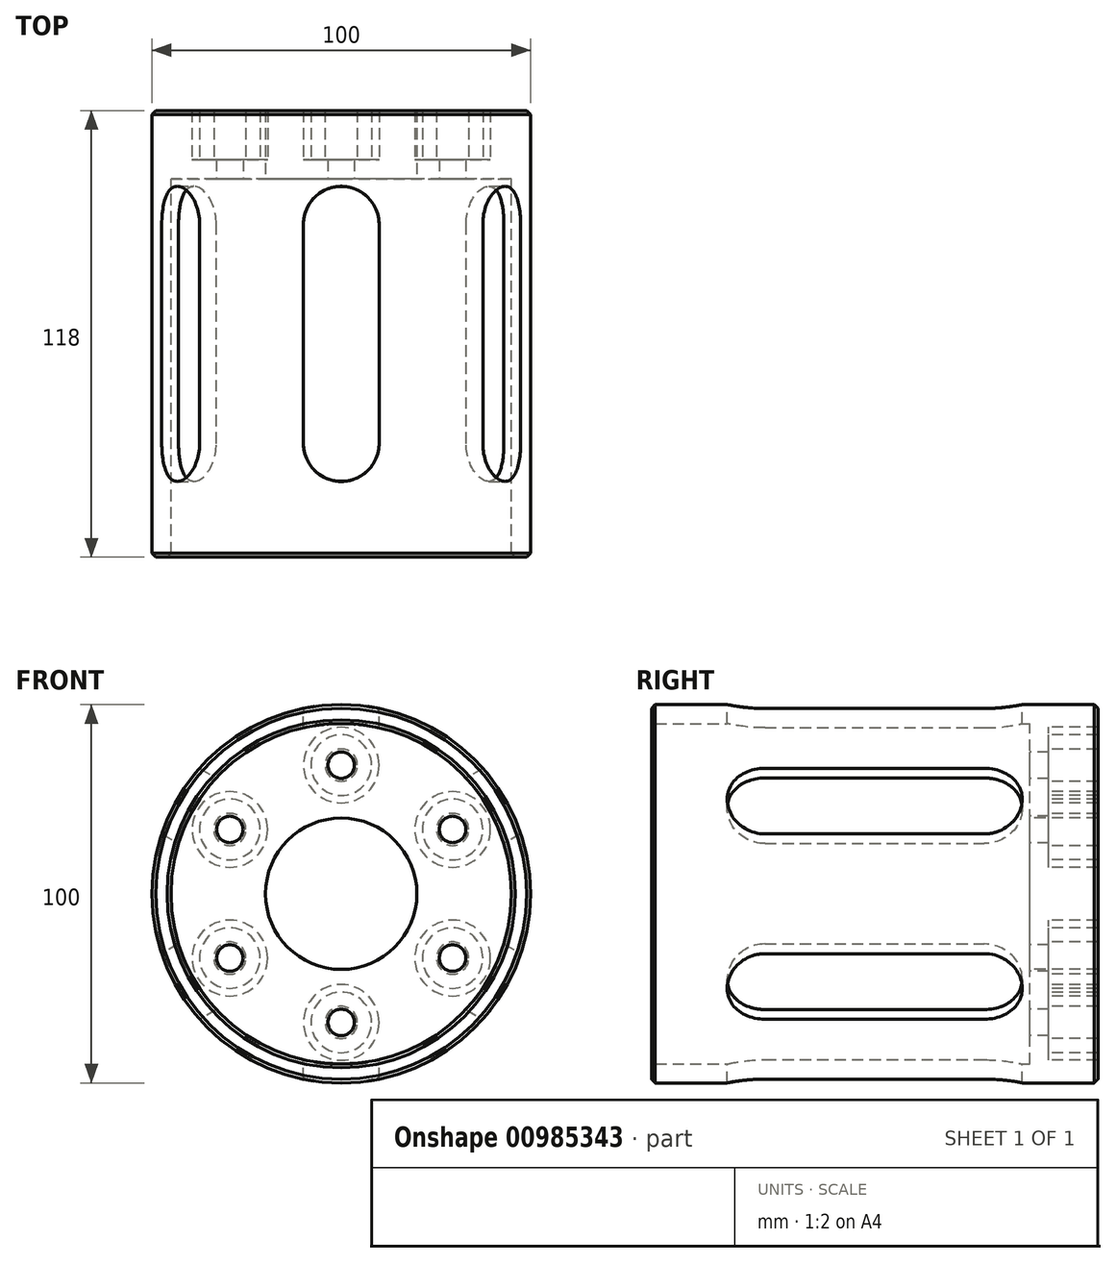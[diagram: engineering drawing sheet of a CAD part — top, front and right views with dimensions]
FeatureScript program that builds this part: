
annotation { "Feature Type Name" : "Feature", "Feature Type Description" : "" }
export const myFeature = defineFeature(function(context is Context, id is Id, definition is map)
    precondition{}
    {
        {
            var Q0;
            Q0=qCreatedBy(makeId("Top.planeOp"),FACE);
            var sketch = newSketch(context, id + "F0", { "sketchPlane" : qUnion([Q0])});
            skLineSegment(sketch, "E0", {"start": v(0, 60.4) * mm, "end": v(0, -60.4) * mm, "construction": true});
            skSolve(sketch);
        }
        {
            var Q0;
            Q0=qCreatedBy(makeId("Front.planeOp"),FACE);
            var sketch = newSketch(context, id + "F1", { "sketchPlane" : qUnion([Q0])});
            skCircle(sketch, "E1", {"center": v(0, 0) * mm, "radius": 50 * mm});
            skCircle(sketch, "E2", {"center": v(0, 34) * mm, "radius": 10 * mm});
            skCircle(sketch, "E3", {"center": v(0, 34) * mm, "radius": 4.25 * mm});
            skCircle(sketch, "E4", {"center": v(0, 34) * mm, "radius": 8 * mm});
            skCircle(sketch, "E5", {"center": v(0, 0) * mm, "radius": 20 * mm});
            skCircle(sketch, "E6", {"center": v(0, 0) * mm, "radius": 45 * mm});
            skCircle(sketch, "E7", {"center": v(0, 34) * mm, "radius": 3.5 * mm});
            skCircle(sketch, "E8.1.0", {"center": v(-29.44, 17) * mm, "radius": 3.5 * mm});
            skCircle(sketch, "E8.1.1", {"center": v(-29.44, 17) * mm, "radius": 4.25 * mm});
            skCircle(sketch, "E8.1.2", {"center": v(-29.44, 17) * mm, "radius": 10 * mm});
            skCircle(sketch, "E8.1.3", {"center": v(-29.44, 17) * mm, "radius": 8 * mm});
            skCircle(sketch, "E8.2.0", {"center": v(-29.44, -17) * mm, "radius": 3.5 * mm});
            skCircle(sketch, "E8.2.1", {"center": v(-29.44, -17) * mm, "radius": 4.25 * mm});
            skCircle(sketch, "E8.2.2", {"center": v(-29.44, -17) * mm, "radius": 10 * mm});
            skCircle(sketch, "E8.2.3", {"center": v(-29.44, -17) * mm, "radius": 8 * mm});
            skCircle(sketch, "E8.3.0", {"center": v(0, -34) * mm, "radius": 3.5 * mm});
            skCircle(sketch, "E8.3.1", {"center": v(0, -34) * mm, "radius": 4.25 * mm});
            skCircle(sketch, "E8.3.2", {"center": v(0, -34) * mm, "radius": 10 * mm});
            skCircle(sketch, "E8.3.3", {"center": v(0, -34) * mm, "radius": 8 * mm});
            skCircle(sketch, "E8.4.0", {"center": v(29.44, -17) * mm, "radius": 3.5 * mm});
            skCircle(sketch, "E8.4.1", {"center": v(29.44, -17) * mm, "radius": 4.25 * mm});
            skCircle(sketch, "E8.4.2", {"center": v(29.44, -17) * mm, "radius": 10 * mm});
            skCircle(sketch, "E8.4.3", {"center": v(29.44, -17) * mm, "radius": 8 * mm});
            skCircle(sketch, "E8.5.0", {"center": v(29.44, 17) * mm, "radius": 3.5 * mm});
            skCircle(sketch, "E8.5.1", {"center": v(29.44, 17) * mm, "radius": 4.25 * mm});
            skCircle(sketch, "E8.5.2", {"center": v(29.44, 17) * mm, "radius": 10 * mm});
            skCircle(sketch, "E8.5.3", {"center": v(29.44, 17) * mm, "radius": 8 * mm});
            skSolve(sketch);
        }
        {
            var Q0;
            Q0=makeQuery(id+"F1.imprint","IMPRINT",FACE,{"disambiguationData":[TD([[makeQuery(id+"F1.imprint","IMPRINT",EDGE,{"derivedFrom":sQuery(id+"F1.wireOp",EDGE,"E2")}),-1.0]])]});
            var Q1;
            Q1=makeQuery(id+"F1.imprint","IMPRINT",FACE,{"disambiguationData":[TD([[makeQuery(id+"F1.imprint","IMPRINT",EDGE,{"derivedFrom":sQuery(id+"F1.wireOp",EDGE,"E8.1.1")}),-1.0]])]});
            var Q2;
            Q2=makeQuery(id+"F1.imprint","IMPRINT",FACE,{"disambiguationData":[TD([[makeQuery(id+"F1.imprint","IMPRINT",EDGE,{"derivedFrom":sQuery(id+"F1.wireOp",EDGE,"E3")}),-1.0]])]});
            var Q3;
            Q3=makeQuery(id+"F1.imprint","IMPRINT",FACE,{"disambiguationData":[TD([[makeQuery(id+"F1.imprint","IMPRINT",EDGE,{"derivedFrom":sQuery(id+"F1.wireOp",EDGE,"E8.5.1")}),-1.0]])]});
            var Q4;
            Q4=makeQuery(id+"F1.imprint","IMPRINT",FACE,{"disambiguationData":[TD([[makeQuery(id+"F1.imprint","IMPRINT",EDGE,{"derivedFrom":sQuery(id+"F1.wireOp",EDGE,"E8.2.1")}),-1.0]])]});
            var Q5;
            Q5=makeQuery(id+"F1.imprint","IMPRINT",FACE,{"disambiguationData":[TD([[makeQuery(id+"F1.imprint","IMPRINT",EDGE,{"derivedFrom":sQuery(id+"F1.wireOp",EDGE,"E8.3.1")}),-1.0]])]});
            var Q6;
            Q6=makeQuery(id+"F1.imprint","IMPRINT",FACE,{"disambiguationData":[TD([[makeQuery(id+"F1.imprint","IMPRINT",EDGE,{"derivedFrom":sQuery(id+"F1.wireOp",EDGE,"E8.4.1")}),-1.0]])]});
            var Q7;
            Q7=makeQuery(id+"F1.imprint","IMPRINT",FACE,{"disambiguationData":[TD([[makeQuery(id+"F1.imprint","IMPRINT",EDGE,{"derivedFrom":sQuery(id+"F1.wireOp",EDGE,"E1")}),1.0]])]});
            extrude(context, id + "F2", {"entities" : qUnion([Q0, Q1, Q2, Q3, Q4, Q5, Q6, Q7]), "oppositeDirection" : true, "depth" : 18 * mm});
        }
        {
            var Q0;
            Q0=makeQuery(id+"F1.imprint","IMPRINT",FACE,{"disambiguationData":[TD([[makeQuery(id+"F1.imprint","IMPRINT",EDGE,{"derivedFrom":sQuery(id+"F1.wireOp",EDGE,"E2")}),1.0]])]});
            var Q1;
            Q1=makeQuery(id+"F1.imprint","IMPRINT",FACE,{"disambiguationData":[TD([[makeQuery(id+"F1.imprint","IMPRINT",EDGE,{"derivedFrom":sQuery(id+"F1.wireOp",EDGE,"E8.1.2")}),1.0]])]});
            var Q2;
            Q2=makeQuery(id+"F1.imprint","IMPRINT",FACE,{"disambiguationData":[TD([[makeQuery(id+"F1.imprint","IMPRINT",EDGE,{"derivedFrom":sQuery(id+"F1.wireOp",EDGE,"E8.2.2")}),1.0]])]});
            var Q3;
            Q3=makeQuery(id+"F1.imprint","IMPRINT",FACE,{"disambiguationData":[TD([[makeQuery(id+"F1.imprint","IMPRINT",EDGE,{"derivedFrom":sQuery(id+"F1.wireOp",EDGE,"E8.3.2")}),1.0]])]});
            var Q4;
            Q4=makeQuery(id+"F1.imprint","IMPRINT",FACE,{"disambiguationData":[TD([[makeQuery(id+"F1.imprint","IMPRINT",EDGE,{"derivedFrom":sQuery(id+"F1.wireOp",EDGE,"E8.4.2")}),1.0]])]});
            var Q5;
            Q5=makeQuery(id+"F1.imprint","IMPRINT",FACE,{"disambiguationData":[TD([[makeQuery(id+"F1.imprint","IMPRINT",EDGE,{"derivedFrom":sQuery(id+"F1.wireOp",EDGE,"E8.5.2")}),1.0]])]});
            var Q6;
            Q6=makeQuery(id+"F1.imprint","IMPRINT",FACE,{"disambiguationData":[TD([[makeQuery(id+"F1.imprint","IMPRINT",EDGE,{"derivedFrom":sQuery(id+"F1.wireOp",EDGE,"E8.1.0")}),-1.0]])]});
            var Q7;
            Q7=makeQuery(id+"F1.imprint","IMPRINT",FACE,{"disambiguationData":[TD([[makeQuery(id+"F1.imprint","IMPRINT",EDGE,{"derivedFrom":sQuery(id+"F1.wireOp",EDGE,"E3")}),1.0]])]});
            var Q8;
            Q8=makeQuery(id+"F1.imprint","IMPRINT",FACE,{"disambiguationData":[TD([[makeQuery(id+"F1.imprint","IMPRINT",EDGE,{"derivedFrom":sQuery(id+"F1.wireOp",EDGE,"E8.5.0")}),-1.0]])]});
            var Q9;
            Q9=makeQuery(id+"F1.imprint","IMPRINT",FACE,{"disambiguationData":[TD([[makeQuery(id+"F1.imprint","IMPRINT",EDGE,{"derivedFrom":sQuery(id+"F1.wireOp",EDGE,"E8.2.0")}),-1.0]])]});
            var Q10;
            Q10=makeQuery(id+"F1.imprint","IMPRINT",FACE,{"disambiguationData":[TD([[makeQuery(id+"F1.imprint","IMPRINT",EDGE,{"derivedFrom":sQuery(id+"F1.wireOp",EDGE,"E8.3.0")}),-1.0]])]});
            var Q11;
            Q11=makeQuery(id+"F1.imprint","IMPRINT",FACE,{"disambiguationData":[TD([[makeQuery(id+"F1.imprint","IMPRINT",EDGE,{"derivedFrom":sQuery(id+"F1.wireOp",EDGE,"E8.4.0")}),-1.0]])]});
            extrude(context, id + "F3", {"entities" : qUnion([Q0, Q1, Q2, Q3, Q4, Q5, Q6, Q7, Q8, Q9, Q10, Q11]), "operationType" : NewBodyOperationType.ADD, "oppositeDirection" : true, "depth" : 5 * mm});
        }
        {
            var Q0;
            Q0=makeQuery(id+"F1.imprint","IMPRINT",FACE,{"disambiguationData":[TD([[makeQuery(id+"F1.imprint","IMPRINT",EDGE,{"derivedFrom":sQuery(id+"F1.wireOp",EDGE,"E1")}),1.0]])]});
            extrude(context, id + "F4", {"entities" : qUnion([Q0]), "operationType" : NewBodyOperationType.ADD, "depth" : 100 * mm});
        }
        {
            var Q0;
            Q0=qCreatedBy(makeId("Top.planeOp"),FACE);
            var sketch = newSketch(context, id + "F5", { "sketchPlane" : qUnion([Q0])});
            skArc(sketch, "E9", {"start": v(10, -12) * mm, "mid": v(0, -2) * mm, "end": v(-10, -12) * mm});
            skArc(sketch, "E10", {"start": v(-10, -70) * mm, "mid": v(0, -80) * mm, "end": v(10, -70) * mm});
            skLineSegment(sketch, "E11", {"start": v(-10, -12) * mm, "end": v(-10, -70) * mm});
            skLineSegment(sketch, "E12", {"start": v(10, -12) * mm, "end": v(10, -70) * mm});
            skSolve(sketch);
        }
        {
            var Q0;
            Q0=qSketchRegion(id+"F5",true);
            extrude(context, id + "F6", {"entities" : qUnion([Q0]), "operationType" : NewBodyOperationType.REMOVE, "endBound" : BoundingType.THROUGH_ALL, "oppositeDirection" : true, "depth" : 25 * mm, "hasSecondDirection" : true, "secondDirectionBound" : SecondDirectionBoundingType.THROUGH_ALL, "secondDirectionOppositeDirection" : false, "secondDirectionDepth" : 25 * mm});
        }
        {
            var Q0;
            Q0=sQuery(id+"F0.wireOp",EDGE,"E0");
            var Q1;
            Q1=qCreatedBy(makeId("Top.planeOp"),FACE);
            cPlane(context, id + "F7", {"entities" : qUnion([Q0, Q1]), "cplaneType" : CPlaneType.LINE_ANGLE, "offset" : 25 * mm, "angle" : 60 * degree, "width" : 150 * mm, "height" : 150 * mm});
        }
        {
            var Q0;
            Q0=qCreatedBy(id+"F7.planeOp",FACE);
            var sketch = newSketch(context, id + "F8", { "sketchPlane" : qUnion([Q0])});
            skLineSegment(sketch, "E13", {"start": v(-12, -10) * mm, "end": v(-70, -10) * mm});
            skLineSegment(sketch, "E14", {"start": v(-70, 10) * mm, "end": v(-12, 10) * mm});
            skArc(sketch, "E15", {"start": v(-12, -10) * mm, "mid": v(-2, 0) * mm, "end": v(-12, 10) * mm});
            skArc(sketch, "E16", {"start": v(-70, -10) * mm, "mid": v(-80, 0) * mm, "end": v(-70, 10) * mm});
            skSolve(sketch);
        }
        {
            var Q0;
            Q0=qSketchRegion(id+"F8",true);
            extrude(context, id + "F9", {"entities" : qUnion([Q0]), "operationType" : NewBodyOperationType.REMOVE, "endBound" : BoundingType.THROUGH_ALL, "oppositeDirection" : true, "depth" : 25 * mm, "hasSecondDirection" : true, "secondDirectionBound" : SecondDirectionBoundingType.THROUGH_ALL, "secondDirectionOppositeDirection" : false, "secondDirectionDepth" : 25 * mm});
        }
        {
            var Q0;
            Q0=qCreatedBy(makeId("Top.planeOp"),FACE);
            var Q1;
            Q1=sQuery(id+"F0.wireOp",EDGE,"E0");
            cPlane(context, id + "F10", {"entities" : qUnion([Q0, Q1]), "cplaneType" : CPlaneType.LINE_ANGLE, "offset" : 25 * mm, "angle" : 300 * degree, "width" : 150 * mm, "height" : 150 * mm});
        }
        {
            var Q0;
            Q0=qCreatedBy(id+"F10.planeOp",FACE);
            var sketch = newSketch(context, id + "F11", { "sketchPlane" : qUnion([Q0])});
            skLineSegment(sketch, "E17.bottom", {"start": v(12, 10) * mm, "end": v(70, 10) * mm});
            skLineSegment(sketch, "E17.top", {"start": v(12, -10) * mm, "end": v(70, -10) * mm});
            skArc(sketch, "E18", {"start": v(70, 10) * mm, "mid": v(80, 0) * mm, "end": v(70, -10) * mm});
            skArc(sketch, "E19", {"start": v(12, -10) * mm, "mid": v(2, 0) * mm, "end": v(12, 10) * mm});
            skSolve(sketch);
        }
        {
            var Q0;
            Q0=qSketchRegion(id+"F11",true);
            extrude(context, id + "F12", {"entities" : qUnion([Q0]), "operationType" : NewBodyOperationType.REMOVE, "endBound" : BoundingType.THROUGH_ALL, "oppositeDirection" : true, "depth" : 25 * mm, "hasSecondDirection" : true, "secondDirectionBound" : SecondDirectionBoundingType.THROUGH_ALL, "secondDirectionOppositeDirection" : false, "secondDirectionDepth" : 25 * mm});
        }
        {
            var Q0;
            Q0=makeQuery(id+"F4.opExtrude","CAP_EDGE",EDGE,{"disambiguationData":[OSD([sQuery(id+"F1.wireOp",EDGE,"E6")])],"isStart":false});
            var Q1;
            Q1=makeQuery(id+"F4.opExtrude","CAP_EDGE",EDGE,{"disambiguationData":[OSD([sQuery(id+"F1.wireOp",EDGE,"E1")])],"isStart":false});
            var Q2;
            Q2=makeQuery(id+"F2.opExtrude","CAP_EDGE",EDGE,{"disambiguationData":[OSD([sQuery(id+"F1.wireOp",EDGE,"E1")])],"isStart":false});
            chamfer(context, id + "F13", {"entities" : qUnion([Q0, Q1, Q2]), "width" : 1 * mm, "tangentPropagation" : true});
        }
    });
